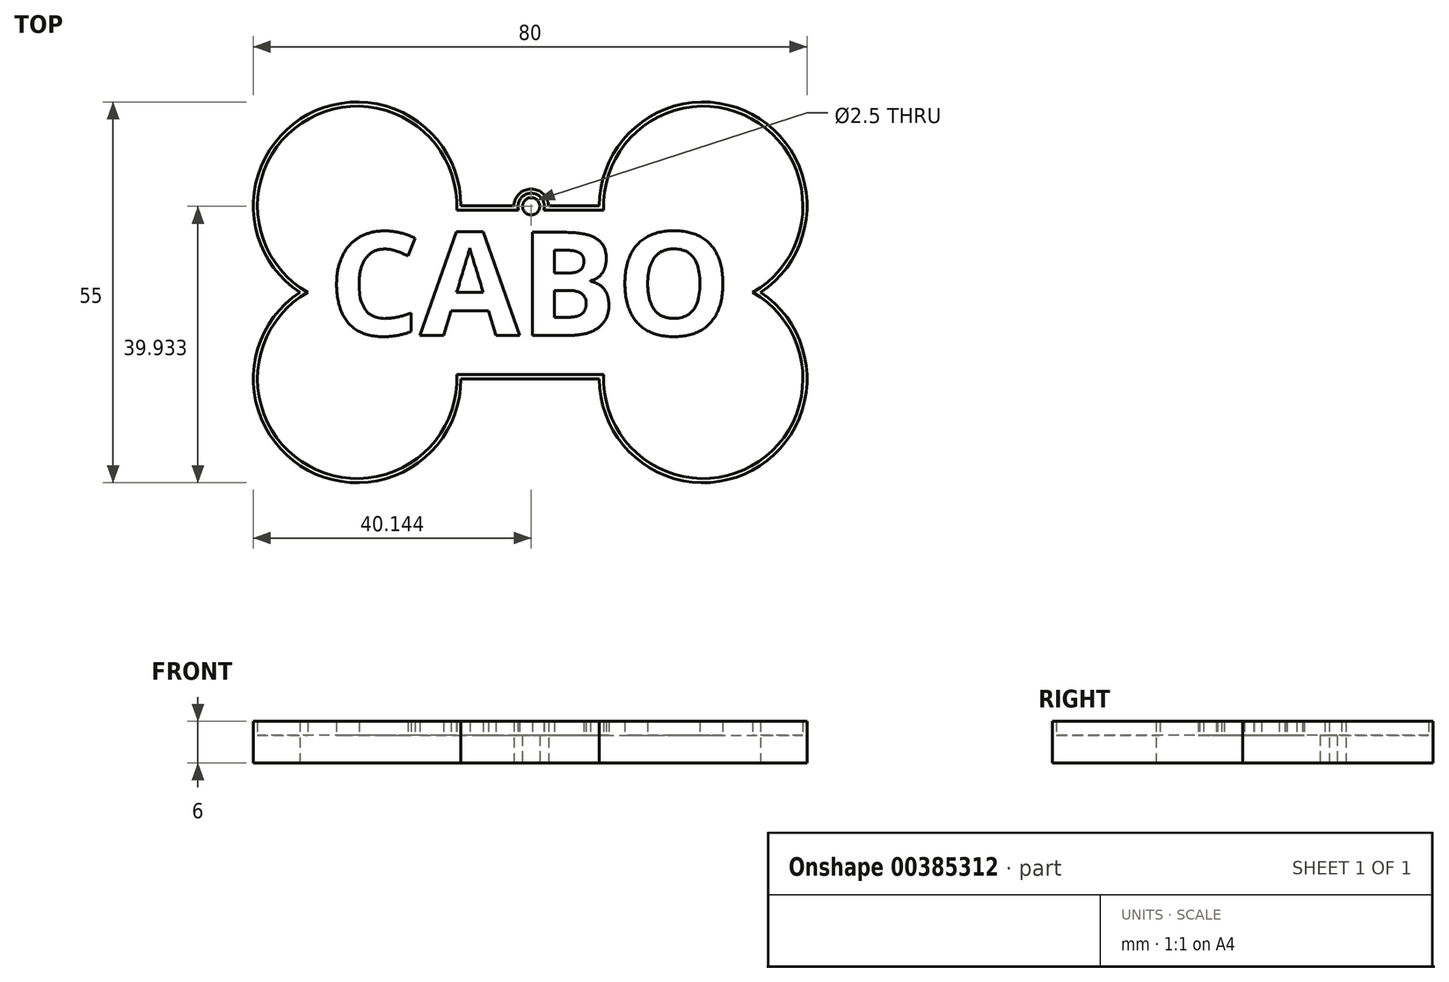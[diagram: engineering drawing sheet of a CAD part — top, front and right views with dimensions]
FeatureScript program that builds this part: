
annotation { "Feature Type Name" : "Feature", "Feature Type Description" : "" }
export const myFeature = defineFeature(function(context is Context, id is Id, definition is map)
    precondition{}
    {
        {
            var Q0;
            Q0=qCreatedBy(makeId("Top.planeOp"),FACE);
            var sketch = newSketch(context, id + "F0", { "sketchPlane" : qUnion([Q0])});
            skLineSegment(sketch, "E0.bottom", {"start": v(-10, 12.5) * mm, "end": v(-2.36, 12.5) * mm});
            skLineSegment(sketch, "E0.top", {"start": v(-10, -12.5) * mm, "end": v(10, -12.5) * mm});
            skArc(sketch, "E1", {"start": v(-10, 12.5) * mm, "mid": v(-32.1, 25.72) * mm, "end": v(-33.3, 0) * mm});
            skArc(sketch, "E2", {"start": v(33.3, 0) * mm, "mid": v(32.1, 25.72) * mm, "end": v(10, 12.5) * mm});
            skArc(sketch, "E3", {"start": v(-33.3, 0) * mm, "mid": v(-32.1, -25.72) * mm, "end": v(-10, -12.5) * mm});
            skArc(sketch, "E4", {"start": v(10, -12.5) * mm, "mid": v(32.1, -25.72) * mm, "end": v(33.3, 0) * mm});
            skArc(sketch, "E5", {"start": v(2.64, 12.5) * mm, "mid": v(0.14, 14.93) * mm, "end": v(-2.36, 12.5) * mm});
            skCircle(sketch, "E6", {"center": v(0.14, 12.43) * mm, "radius": 1.25 * mm});
            skLineSegment(sketch, "E7.trimOffspring", {"start": v(2.64, 12.5) * mm, "end": v(10, 12.5) * mm});
            skSolve(sketch);
        }
        {
            var Q0;
            Q0 = qSketchRegion(id + "F0", true);
            extrude(context, id + "F1", {"entities" : qUnion([Q0]), "depth" : 4 * mm});
        }
        {
            var Q0;
            Q0=makeQuery(id+"F1.opExtrude","CAP_FACE",FACE,{"disambiguationData":[OSD([sQuery(id+"F0.wireOp",EDGE,"E0.bottom"),sQuery(id+"F0.wireOp",EDGE,"E0.top"),sQuery(id+"F0.wireOp",EDGE,"E1"),sQuery(id+"F0.wireOp",EDGE,"E2"),sQuery(id+"F0.wireOp",EDGE,"E3"),sQuery(id+"F0.wireOp",EDGE,"E4"),sQuery(id+"F0.wireOp",EDGE,"E5"),sQuery(id+"F0.wireOp",EDGE,"E6"),sQuery(id+"F0.wireOp",EDGE,"E7.trimOffspring")])],"isStart":false});
            var sketch = newSketch(context, id + "F2", { "sketchPlane" : qUnion([Q0])});
            skArc(sketch, "E8.0", {"start": v(-32.15, 0) * mm, "mid": v(-31.96, -25.1) * mm, "end": v(-10.61, -11.9) * mm});
            skArc(sketch, "E8.1", {"start": v(-10.61, 11.9) * mm, "mid": v(-31.96, 25.1) * mm, "end": v(-32.15, 0) * mm});
            skLineSegment(sketch, "E8.2", {"start": v(-10.61, -11.9) * mm, "end": v(10.61, -11.9) * mm});
            skLineSegment(sketch, "E8.3", {"start": v(-1.68, 11.9) * mm, "end": v(-10.61, 11.9) * mm});
            skArc(sketch, "E8.4", {"start": v(10.61, -11.9) * mm, "mid": v(31.96, -25.1) * mm, "end": v(32.15, 0) * mm});
            skArc(sketch, "E8.5", {"start": v(32.15, 0) * mm, "mid": v(31.96, 25.1) * mm, "end": v(10.61, 11.9) * mm});
            skLineSegment(sketch, "E8.6", {"start": v(10.61, 11.9) * mm, "end": v(1.97, 11.9) * mm});
            skArc(sketch, "E8.7", {"start": v(1.97, 11.9) * mm, "mid": v(0.14, 14.33) * mm, "end": v(-1.68, 11.9) * mm});
            skSolve(sketch);
        }
        {
            var Q0;
            Q0=makeQuery(id+"F2.imprint","IMPRINT",FACE,{"disambiguationData":[TD([[makeQuery(id+"F2.imprint","IMPRINT",EDGE,{"derivedFrom":sQuery(id+"F2.wireOp",EDGE,"E8.0")}),-1.0]])]});
            extrude(context, id + "F3", {"entities" : qUnion([Q0]), "operationType" : NewBodyOperationType.ADD, "depth" : 2 * mm});
        }
        {
            var Q0;
            Q0=makeQuery(id+"F1.opExtrude","CAP_FACE",FACE,{"disambiguationData":[OSD([sQuery(id+"F0.wireOp",EDGE,"E0.bottom"),sQuery(id+"F0.wireOp",EDGE,"E0.top"),sQuery(id+"F0.wireOp",EDGE,"E1"),sQuery(id+"F0.wireOp",EDGE,"E2"),sQuery(id+"F0.wireOp",EDGE,"E3"),sQuery(id+"F0.wireOp",EDGE,"E4"),sQuery(id+"F0.wireOp",EDGE,"E5"),sQuery(id+"F0.wireOp",EDGE,"E6"),sQuery(id+"F0.wireOp",EDGE,"E7.trimOffspring")])],"isStart":false});
            var sketch = newSketch(context, id + "F4", { "sketchPlane" : qUnion([Q0])});
            skText(sketch, "E9", { "text": "CABO", "fontName": "OpenSans-Bold.ttf"});
            const initialGuessF4  = {"E9": [-0.02918, -0.0062, 1, 0, 0.015]};
            skSetInitialGuess(sketch, initialGuessF4);
            skSolve(sketch);
        }
        {
            var Q0;
            Q0=makeQuery(id+"F4.imprint","IMPRINT",FACE,{"disambiguationData":[TD([[makeQuery(id+"F4.imprint","IMPRINT",EDGE,{"derivedFrom":sQuery(id+"F4.wireOp",EDGE,"E9.sketch_text.stroke-15")}),-1.0]])]});
            var sketch = newSketch(context, id + "F5", { "sketchPlane" : qUnion([Q0])});
            skSolve(sketch);
        }
        {
            var Q0;
            Q0 = qSketchRegion(id + "F5", true);
            var Q1;
            Q1 = qSketchRegion(id + "F4", true);
            extrude(context, id + "F6", {"entities" : qUnion([Q0, Q1]), "operationType" : NewBodyOperationType.ADD, "depth" : 2 * mm});
        }
    });
